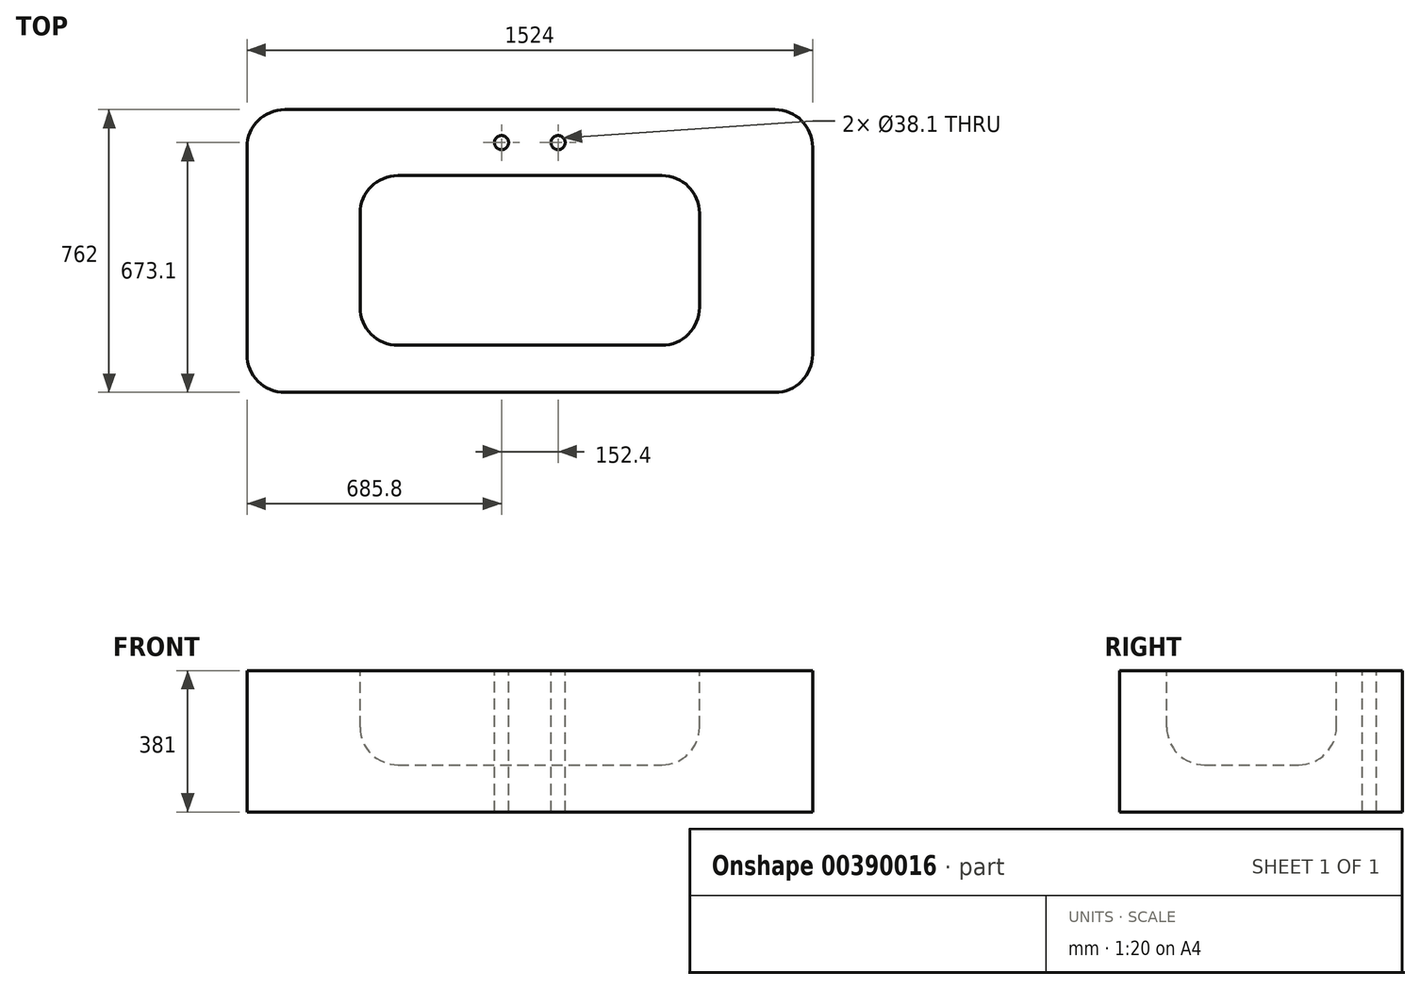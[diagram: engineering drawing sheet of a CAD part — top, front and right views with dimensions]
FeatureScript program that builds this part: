
annotation { "Feature Type Name" : "Feature", "Feature Type Description" : "" }
export const myFeature = defineFeature(function(context is Context, id is Id, definition is map)
    precondition{}
    {
        {
            var Q0;
            Q0=qCreatedBy(makeId("Top.planeOp"),FACE);
            var sketch = newSketch(context, id + "F0", { "sketchPlane" : qUnion([Q0])});
            skLineSegment(sketch, "E0.bottom", {"start": v(762, 381) * mm, "end": v(-762, 381) * mm});
            skLineSegment(sketch, "E0.top", {"start": v(762, -381) * mm, "end": v(-762, -381) * mm});
            skLineSegment(sketch, "E0.left", {"start": v(762, 381) * mm, "end": v(762, -381) * mm});
            skLineSegment(sketch, "E0.right", {"start": v(-762, 381) * mm, "end": v(-762, -381) * mm});
            skPoint(sketch, "E0.middle", {"position": v(0, 0) * mm});
            skSolve(sketch);
        }
        {
            var Q0;
            Q0 = qSketchRegion(id + "F0", true);
            extrude(context, id + "F1", {"entities" : qUnion([Q0]), "depth" : 381 * mm});
        }
        {
            var Q0;
            Q0=makeQuery(id+"F1.opExtrude","SWEPT_EDGE",EDGE,{"disambiguationData":[OSD([sQuery(id+"F0.wireOp",EDGE,"E0.bottom"),sQuery(id+"F0.wireOp",EDGE,"E0.right")])]});
            var Q1;
            Q1=makeQuery(id+"F1.opExtrude","SWEPT_EDGE",EDGE,{"disambiguationData":[OSD([sQuery(id+"F0.wireOp",EDGE,"E0.top"),sQuery(id+"F0.wireOp",EDGE,"E0.right")])]});
            var Q2;
            Q2=makeQuery(id+"F1.opExtrude","SWEPT_EDGE",EDGE,{"disambiguationData":[OSD([sQuery(id+"F0.wireOp",EDGE,"E0.top"),sQuery(id+"F0.wireOp",EDGE,"E0.left")])]});
            var Q3;
            Q3=makeQuery(id+"F1.opExtrude","SWEPT_EDGE",EDGE,{"disambiguationData":[OSD([sQuery(id+"F0.wireOp",EDGE,"E0.bottom"),sQuery(id+"F0.wireOp",EDGE,"E0.left")])]});
            fillet(context, id + "F2", {"entities" : qUnion([Q0, Q1, Q2, Q3]), "radius" : 101.6 * mm, "tangentPropagation" : true, "allowEdgeOverflow" : false});
        }
        {
            var Q0;
            Q0=makeQuery(id+"F1.opExtrude","CAP_FACE",FACE,{"disambiguationData":[OSD([sQuery(id+"F0.wireOp",EDGE,"E0.bottom"),sQuery(id+"F0.wireOp",EDGE,"E0.top"),sQuery(id+"F0.wireOp",EDGE,"E0.left"),sQuery(id+"F0.wireOp",EDGE,"E0.right")])],"isStart":false});
            var sketch = newSketch(context, id + "F3", { "sketchPlane" : qUnion([Q0])});
            skLineSegment(sketch, "E1.bottom", {"start": v(-457.2, -254) * mm, "end": v(457.2, -254) * mm});
            skLineSegment(sketch, "E1.top", {"start": v(-457.2, 203.2) * mm, "end": v(457.2, 203.2) * mm});
            skLineSegment(sketch, "E1.left", {"start": v(-457.2, -254) * mm, "end": v(-457.2, 203.2) * mm});
            skLineSegment(sketch, "E1.right", {"start": v(457.2, -254) * mm, "end": v(457.2, 203.2) * mm});
            skSolve(sketch);
        }
        {
            var Q0;
            Q0 = qSketchRegion(id + "F3", true);
            extrude(context, id + "F4", {"entities" : qUnion([Q0]), "operationType" : NewBodyOperationType.REMOVE, "oppositeDirection" : true, "depth" : 254 * mm});
        }
        {
            var Q0;
            Q0=makeQuery(id+"F4.boolean.opBoolean","COPY",EDGE,{"derivedFrom":makeQuery(id+"F4.opExtrude","SWEPT_EDGE",EDGE,{"disambiguationData":[OSD([sQuery(id+"F3.wireOp",EDGE,"E1.top"),sQuery(id+"F3.wireOp",EDGE,"E1.left")])]})});
            var Q1;
            Q1=makeQuery(id+"F4.boolean.opBoolean","COPY",EDGE,{"derivedFrom":makeQuery(id+"F4.opExtrude","SWEPT_EDGE",EDGE,{"disambiguationData":[OSD([sQuery(id+"F3.wireOp",EDGE,"E1.top"),sQuery(id+"F3.wireOp",EDGE,"E1.right")])]})});
            var Q2;
            Q2=makeQuery(id+"F4.boolean.opBoolean","COPY",EDGE,{"derivedFrom":makeQuery(id+"F4.opExtrude","SWEPT_EDGE",EDGE,{"disambiguationData":[OSD([sQuery(id+"F3.wireOp",EDGE,"E1.bottom"),sQuery(id+"F3.wireOp",EDGE,"E1.right")])]})});
            var Q3;
            Q3=makeQuery(id+"F4.boolean.opBoolean","COPY",EDGE,{"derivedFrom":makeQuery(id+"F4.opExtrude","SWEPT_EDGE",EDGE,{"disambiguationData":[OSD([sQuery(id+"F3.wireOp",EDGE,"E1.bottom"),sQuery(id+"F3.wireOp",EDGE,"E1.left")])]})});
            var Q4;
            Q4=makeQuery(id+"F4.boolean.opBoolean","COPY",EDGE,{"derivedFrom":makeQuery(id+"F4.opExtrude","CAP_EDGE",EDGE,{"disambiguationData":[OSD([sQuery(id+"F3.wireOp",EDGE,"E1.left")])],"isStart":false})});
            var Q5;
            Q5=makeQuery(id+"F4.boolean.opBoolean","COPY",EDGE,{"derivedFrom":makeQuery(id+"F4.opExtrude","CAP_EDGE",EDGE,{"disambiguationData":[OSD([sQuery(id+"F3.wireOp",EDGE,"E1.bottom")])],"isStart":false})});
            var Q6;
            Q6=makeQuery(id+"F4.boolean.opBoolean","COPY",EDGE,{"derivedFrom":makeQuery(id+"F4.opExtrude","CAP_EDGE",EDGE,{"disambiguationData":[OSD([sQuery(id+"F3.wireOp",EDGE,"E1.right")])],"isStart":false})});
            var Q7;
            Q7=makeQuery(id+"F4.boolean.opBoolean","COPY",EDGE,{"derivedFrom":makeQuery(id+"F4.opExtrude","CAP_EDGE",EDGE,{"disambiguationData":[OSD([sQuery(id+"F3.wireOp",EDGE,"E1.top")])],"isStart":false})});
            fillet(context, id + "F5", {"entities" : qUnion([Q0, Q1, Q2, Q3, Q4, Q5, Q6, Q7]), "radius" : 101.6 * mm, "tangentPropagation" : true, "allowEdgeOverflow" : false});
        }
        {
            var Q0;
            Q0=makeQuery(id+"F1.opExtrude","CAP_FACE",FACE,{"disambiguationData":[OSD([sQuery(id+"F0.wireOp",EDGE,"E0.bottom"),sQuery(id+"F0.wireOp",EDGE,"E0.top"),sQuery(id+"F0.wireOp",EDGE,"E0.left"),sQuery(id+"F0.wireOp",EDGE,"E0.right")])],"isStart":false});
            var sketch = newSketch(context, id + "F6", { "sketchPlane" : qUnion([Q0])});
            skCircle(sketch, "E2", {"center": v(-76.2, 292.1) * mm, "radius": 19.05 * mm});
            skSolve(sketch);
        }
        {
            var Q0;
            Q0 = qSketchRegion(id + "F6", true);
            extrude(context, id + "F7", {"entities" : qUnion([Q0]), "operationType" : NewBodyOperationType.REMOVE, "endBound" : BoundingType.THROUGH_ALL, "oppositeDirection" : true, "depth" : 25.4 * mm});
        }
        {
            var Q0;
            Q0=makeQuery(id+"F1.opExtrude","CAP_FACE",FACE,{"disambiguationData":[OSD([sQuery(id+"F0.wireOp",EDGE,"E0.bottom"),sQuery(id+"F0.wireOp",EDGE,"E0.top"),sQuery(id+"F0.wireOp",EDGE,"E0.left"),sQuery(id+"F0.wireOp",EDGE,"E0.right")])],"isStart":false});
            var sketch = newSketch(context, id + "F8", { "sketchPlane" : qUnion([Q0])});
            skCircle(sketch, "E3", {"center": v(76.2, 292.1) * mm, "radius": 19.05 * mm});
            skSolve(sketch);
        }
        {
            var Q0;
            Q0 = qSketchRegion(id + "F8", true);
            extrude(context, id + "F9", {"entities" : qUnion([Q0]), "operationType" : NewBodyOperationType.REMOVE, "endBound" : BoundingType.THROUGH_ALL, "oppositeDirection" : true, "depth" : 25.4 * mm});
        }
    });
